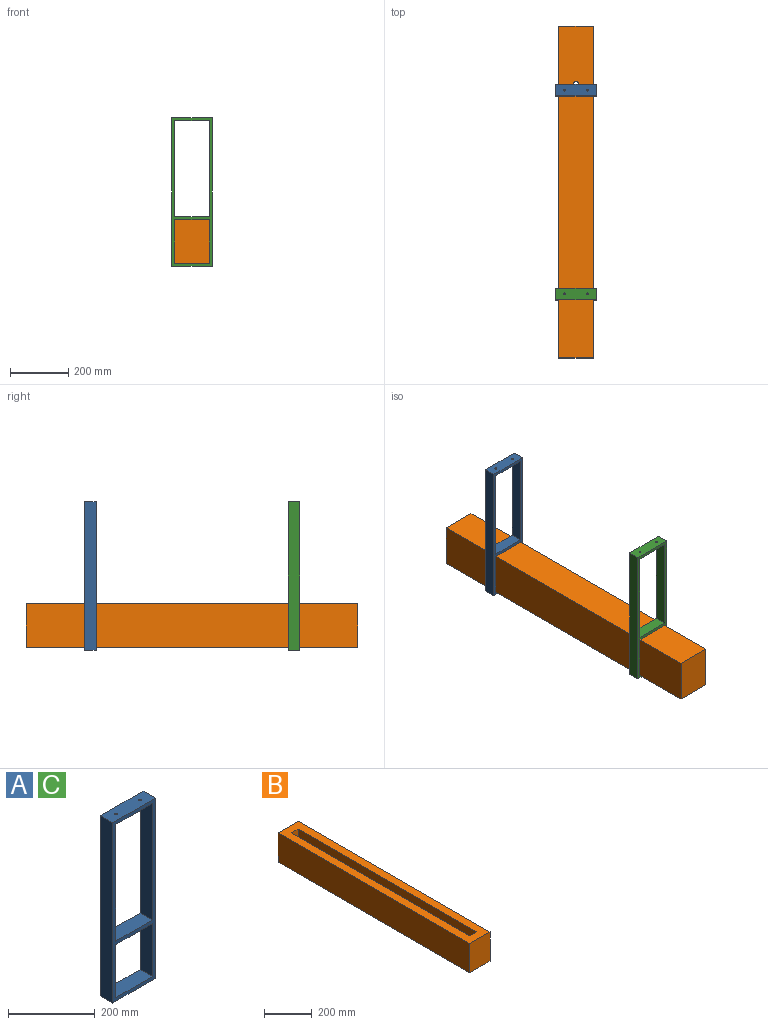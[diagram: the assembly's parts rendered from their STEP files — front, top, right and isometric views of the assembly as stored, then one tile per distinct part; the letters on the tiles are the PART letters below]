
ASSEMBLY  parts=3 mates=2
PART A: 16 faces, bbox 140x40x510 mm
  f0: plane 510x40mm, normal (1,0,0), area 20400mm2, adj f1,f11,f12,f13
  f1: plane 140x40mm, normal (0,0,1), area 5533.6mm2, adj f0,f2,f12,f13,f14,f15
  f2: plane 510x40mm, normal (-1,0,0), area 20400mm2, adj f1,f11,f12,f13
  f3: plane 120x40mm, normal (0,0,-1), area 4800mm2, adj f4,f9,f12,f13
  f4: plane 150x40mm, normal (-1,0,0), area 6000mm2, adj f3,f5,f12,f13
  f5: plane 120x40mm, normal (0,0,1), area 4800mm2, adj f4,f9,f12,f13
  f6: plane 330x40mm, normal (-1,0,0), area 13200mm2, adj f7,f10,f12,f13
  f7: plane 120x40mm, normal (0,0,1), area 4800mm2, adj f6,f8,f12,f13
  f8: plane 330x40mm, normal (1,0,0), area 13200mm2, adj f7,f10,f12,f13
  f9: plane 150x40mm, normal (1,0,0), area 6000mm2, adj f3,f5,f12,f13
  f10: plane 120x40mm, normal (0,0,-1), area 4733.6mm2, adj f6,f8,f12,f13,f14,f15
  f11: plane 140x40mm, normal (0,0,-1), area 5600mm2, adj f0,f2,f12,f13
  f12: plane 510x140mm, normal (0,1,0), area 13800mm2, adj f0,f1,f2,f3,f4,f5,f6,f7
  f13: plane 510x140mm, normal (0,-1,0), area 13800mm2, adj f0,f1,f2,f3,f4,f5,f6,f7
  f14: cylinder r=3.25mm len=10mm, axis (0,0,1), area 204.2mm2, adj f1,f10
  f15: cylinder r=3.25mm len=10mm, axis (0,0,1), area 204.2mm2, adj f1,f10
PART B: 12 faces, bbox 120x1140x150 mm
  f0: plane 1140x120mm, normal (0,0,1), area 94400mm2, adj f2,f3,f4,f5,f6,f7,f8,f9
  f1: plane 1140x120mm, normal (0,0,-1), area 136485.8mm2, adj f2,f3,f4,f5,f11
  f2: plane 1140x150mm, normal (1,0,0), area 171000mm2, adj f0,f1,f4,f5
  f3: plane 1140x150mm, normal (-1,0,0), area 171000mm2, adj f0,f1,f4,f5
  f4: plane 150x120mm, normal (0,1,0), area 18000mm2, adj f0,f1,f2,f3
  f5: plane 150x120mm, normal (0,-1,0), area 18000mm2, adj f0,f1,f2,f3
  f6: plane 60x40mm, normal (0,1,0), area 2400mm2, adj f0,f7,f9,f10
  f7: plane 1060x60mm, normal (-1,0,0), area 63600mm2, adj f0,f6,f8,f10
  f8: plane 60x40mm, normal (0,-1,0), area 2400mm2, adj f0,f7,f9,f10
  f9: plane 1060x60mm, normal (1,0,0), area 63600mm2, adj f0,f6,f8,f10
  f10: plane 1060x40mm, normal (0,0,1), area 42085.8mm2, adj f6,f7,f8,f9,f11
  f11: cylinder r=10mm len=90mm, axis (0,0,-1), area 5654.9mm2, adj f1,f10
PART C: same geometry as A
PLACE A t=(230.26,619.07,425.57)mm
PLACE B rot(axis=(0,-1,0),180deg) t=(230.26,-280.08,510.57)mm
PLACE C t=(230.26,-80.93,425.57)mm
MATE fastened B.f1 <-> C.f3  axis (0,0,1) through (230.26,289.07,585.57)mm
MATE fastened B.f1 <-> A.f3  axis (0,0,1) through (230.26,289.07,585.57)mm
